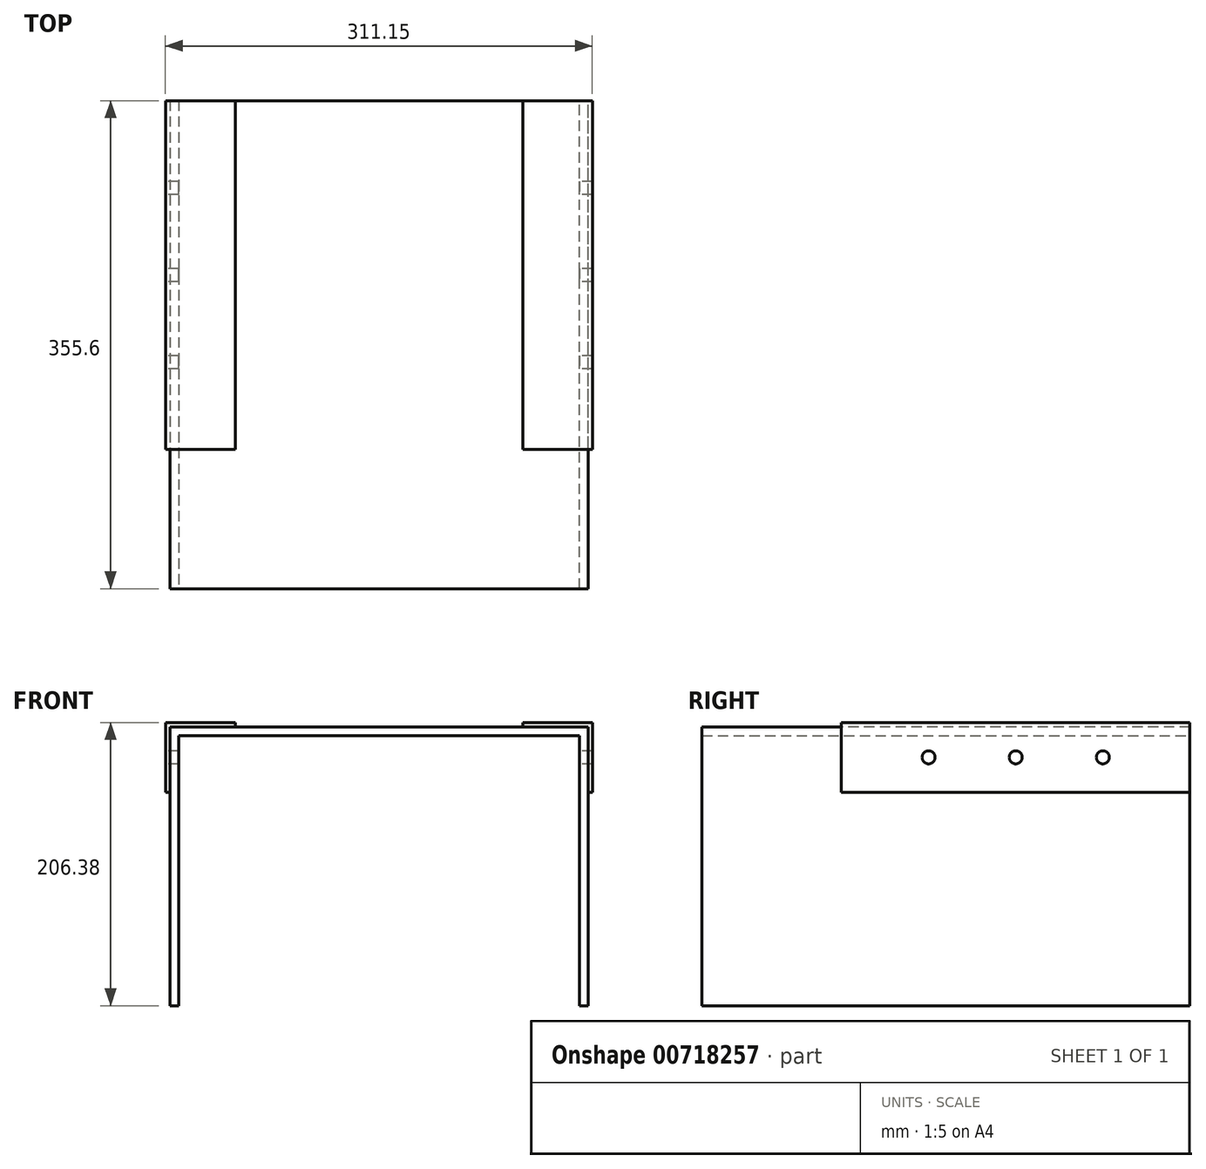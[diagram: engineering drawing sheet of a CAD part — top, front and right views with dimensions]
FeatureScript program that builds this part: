
annotation { "Feature Type Name" : "Feature", "Feature Type Description" : "" }
export const myFeature = defineFeature(function(context is Context, id is Id, definition is map)
    precondition{}
    {
        {
            var Q0;
            Q0=qCreatedBy(makeId("Top.planeOp"),FACE);
            var sketch = newSketch(context, id + "F0", { "sketchPlane" : qUnion([Q0])});
            skLineSegment(sketch, "E0", {"start": v(0, 0) * mm, "end": v(136.23, 0) * mm});
            skLineSegment(sketch, "E1", {"start": v(136.23, 0) * mm, "end": v(136.23, 355.6) * mm});
            skLineSegment(sketch, "E2", {"start": v(136.23, 355.6) * mm, "end": v(-168.57, 355.6) * mm});
            skLineSegment(sketch, "E3", {"start": v(-168.57, 355.6) * mm, "end": v(-168.57, 0) * mm});
            skLineSegment(sketch, "E4", {"start": v(-168.57, 0) * mm, "end": v(0, 0) * mm});
            skSolve(sketch);
        }
        {
            var Q0;
            Q0 = qSketchRegion(id + "F0", true);
            extrude(context, id + "F1", {"entities" : qUnion([Q0]), "depth" : 203.2 * mm, "offsetDistance" : 25.4 * mm});
        }
        {
            var Q0;
            Q0=makeQuery(id+"F1.opExtrude","CAP_FACE",FACE,{"disambiguationData":[OSD([sQuery(id+"F0.wireOp",EDGE,"E0"),sQuery(id+"F0.wireOp",EDGE,"E1"),sQuery(id+"F0.wireOp",EDGE,"E2"),sQuery(id+"F0.wireOp",EDGE,"E3"),sQuery(id+"F0.wireOp",EDGE,"E4")])],"isStart":true});
            shell(context, id + "F2", {"entities" : qUnion([Q0]), "thickness" : 6.35 * mm});
        }
        {
            var Q0;
            Q0=makeQuery(id+"F1.opExtrude","CAP_FACE",FACE,{"disambiguationData":[OSD([sQuery(id+"F0.wireOp",EDGE,"E0"),sQuery(id+"F0.wireOp",EDGE,"E1"),sQuery(id+"F0.wireOp",EDGE,"E2"),sQuery(id+"F0.wireOp",EDGE,"E3"),sQuery(id+"F0.wireOp",EDGE,"E4")])],"isStart":false});
            var sketch = newSketch(context, id + "F3", { "sketchPlane" : qUnion([Q0])});
            skLineSegment(sketch, "E5", {"start": v(-168.57, 101.6) * mm, "end": v(-120.95, 101.6) * mm});
            skLineSegment(sketch, "E6", {"start": v(-120.95, 101.6) * mm, "end": v(-120.95, 355.6) * mm});
            skLineSegment(sketch, "E7", {"start": v(-120.95, 355.6) * mm, "end": v(-168.57, 355.6) * mm});
            skLineSegment(sketch, "E8", {"start": v(-168.57, 355.6) * mm, "end": v(-171.75, 355.6) * mm});
            skLineSegment(sketch, "E9", {"start": v(-171.75, 355.6) * mm, "end": v(-171.75, 101.6) * mm});
            skLineSegment(sketch, "E10", {"start": v(-171.75, 101.6) * mm, "end": v(-168.57, 101.6) * mm});
            skLineSegment(sketch, "E11", {"start": v(136.23, 355.6) * mm, "end": v(88.6, 355.6) * mm});
            skLineSegment(sketch, "E12", {"start": v(88.6, 355.6) * mm, "end": v(88.6, 101.6) * mm});
            skLineSegment(sketch, "E13", {"start": v(88.6, 101.6) * mm, "end": v(136.23, 101.6) * mm});
            skLineSegment(sketch, "E14", {"start": v(136.23, 101.6) * mm, "end": v(139.4, 101.6) * mm});
            skLineSegment(sketch, "E15", {"start": v(139.4, 101.6) * mm, "end": v(139.4, 355.6) * mm});
            skLineSegment(sketch, "E16", {"start": v(139.4, 355.6) * mm, "end": v(136.23, 355.6) * mm});
            skSolve(sketch);
        }
        {
            var Q0;
            Q0 = qSketchRegion(id + "F3", true);
            extrude(context, id + "F4", {"entities" : qUnion([Q0]), "operationType" : NewBodyOperationType.ADD, "depth" : 3.17 * mm, "offsetDistance" : 25.4 * mm});
        }
        {
            var Q0;
            Q0=makeQuery(id+"F1.opExtrude","SWEPT_FACE",FACE,{"disambiguationData":[OSD([sQuery(id+"F0.wireOp",EDGE,"E0"),sQuery(id+"F0.wireOp",EDGE,"E4")])]});
            var sketch = newSketch(context, id + "F5", { "sketchPlane" : qUnion([Q0])});
            skLineSegment(sketch, "E17", {"start": v(-168.57, 0) * mm, "end": v(-162.22, 0) * mm});
            skLineSegment(sketch, "E18", {"start": v(-162.22, 0) * mm, "end": v(-162.22, 196.85) * mm});
            skLineSegment(sketch, "E19", {"start": v(-162.22, 196.85) * mm, "end": v(129.88, 196.85) * mm});
            skLineSegment(sketch, "E20", {"start": v(129.88, 196.85) * mm, "end": v(129.88, 0) * mm});
            skLineSegment(sketch, "E21", {"start": v(129.88, 0) * mm, "end": v(-162.22, 0) * mm});
            skSolve(sketch);
        }
        {
            var Q0;
            Q0 = qSketchRegion(id + "F5", true);
            extrude(context, id + "F6", {"entities" : qUnion([Q0]), "operationType" : NewBodyOperationType.REMOVE, "oppositeDirection" : true, "depth" : 640.08 * mm, "offsetDistance" : 25.4 * mm});
        }
        {
            var Q0;
            Q0=makeQuery(id+"F4.opExtrude","CAP_FACE",FACE,{"disambiguationData":[OSD([sQuery(id+"F3.wireOp",EDGE,"E5"),sQuery(id+"F3.wireOp",EDGE,"E6"),sQuery(id+"F3.wireOp",EDGE,"E7"),sQuery(id+"F3.wireOp",EDGE,"E8"),sQuery(id+"F3.wireOp",EDGE,"E9"),sQuery(id+"F3.wireOp",EDGE,"E10")])],"isStart":true});
            var sketch = newSketch(context, id + "F7", { "sketchPlane" : qUnion([Q0])});
            skLineSegment(sketch, "E22", {"start": v(-171.75, -101.6) * mm, "end": v(-168.57, -101.6) * mm});
            skLineSegment(sketch, "E23", {"start": v(-168.57, -101.6) * mm, "end": v(-168.57, -355.6) * mm});
            skLineSegment(sketch, "E24", {"start": v(-168.57, -355.6) * mm, "end": v(-171.75, -355.6) * mm});
            skLineSegment(sketch, "E25", {"start": v(-171.75, -355.6) * mm, "end": v(-171.75, -101.6) * mm});
            skSolve(sketch);
        }
        {
            var Q0;
            Q0 = qSketchRegion(id + "F7", true);
            extrude(context, id + "F8", {"entities" : qUnion([Q0]), "operationType" : NewBodyOperationType.ADD, "depth" : 47.62 * mm, "offsetDistance" : 25.4 * mm});
        }
        {
            var Q0;
            Q0=makeQuery(id+"F8.boolean.opBoolean","MERGE",FACE,{"derivedFrom":[makeQuery(id+"F4.opExtrude","SWEPT_FACE",FACE,{"disambiguationData":[OSD([sQuery(id+"F3.wireOp",EDGE,"E9")])]}),makeQuery(id+"F8.opExtrude","SWEPT_FACE",FACE,{"disambiguationData":[OSD([sQuery(id+"F7.wireOp",EDGE,"E25")])]})]});
            var sketch = newSketch(context, id + "F9", { "sketchPlane" : qUnion([Q0])});
            skLineSegment(sketch, "E26", {"start": v(-355.6, 180.98) * mm, "end": v(-101.6, 180.98) * mm});
            skCircle(sketch, "E27", {"center": v(-292.1, 180.98) * mm, "radius": 4.76 * mm});
            skCircle(sketch, "E28", {"center": v(-228.6, 180.97) * mm, "radius": 4.76 * mm});
            skCircle(sketch, "E29", {"center": v(-165.1, 180.98) * mm, "radius": 4.76 * mm});
            skSolve(sketch);
        }
        {
            var Q0;
            Q0=makeQuery(id+"F4.opExtrude","CAP_FACE",FACE,{"disambiguationData":[OSD([sQuery(id+"F3.wireOp",EDGE,"E11"),sQuery(id+"F3.wireOp",EDGE,"E12"),sQuery(id+"F3.wireOp",EDGE,"E13"),sQuery(id+"F3.wireOp",EDGE,"E14"),sQuery(id+"F3.wireOp",EDGE,"E15"),sQuery(id+"F3.wireOp",EDGE,"E16")])],"isStart":true});
            var sketch = newSketch(context, id + "F10", { "sketchPlane" : qUnion([Q0])});
            skLineSegment(sketch, "E30", {"start": v(139.4, -101.6) * mm, "end": v(136.23, -101.6) * mm});
            skLineSegment(sketch, "E31", {"start": v(136.23, -101.6) * mm, "end": v(136.23, -355.6) * mm});
            skLineSegment(sketch, "E32", {"start": v(136.23, -355.6) * mm, "end": v(139.4, -355.6) * mm});
            skLineSegment(sketch, "E33", {"start": v(139.4, -355.6) * mm, "end": v(139.4, -101.6) * mm});
            skSolve(sketch);
        }
        {
            var Q0;
            Q0 = qSketchRegion(id + "F10", true);
            extrude(context, id + "F11", {"entities" : qUnion([Q0]), "operationType" : NewBodyOperationType.ADD, "depth" : 47.62 * mm, "offsetDistance" : 25.4 * mm});
        }
        {
            var Q0;
            Q0 = qSketchRegion(id + "F9", true);
            extrude(context, id + "F12", {"entities" : qUnion([Q0]), "operationType" : NewBodyOperationType.REMOVE, "endBound" : BoundingType.THROUGH_ALL, "oppositeDirection" : true, "depth" : 25.4 * mm, "offsetDistance" : 25.4 * mm});
        }
    });
